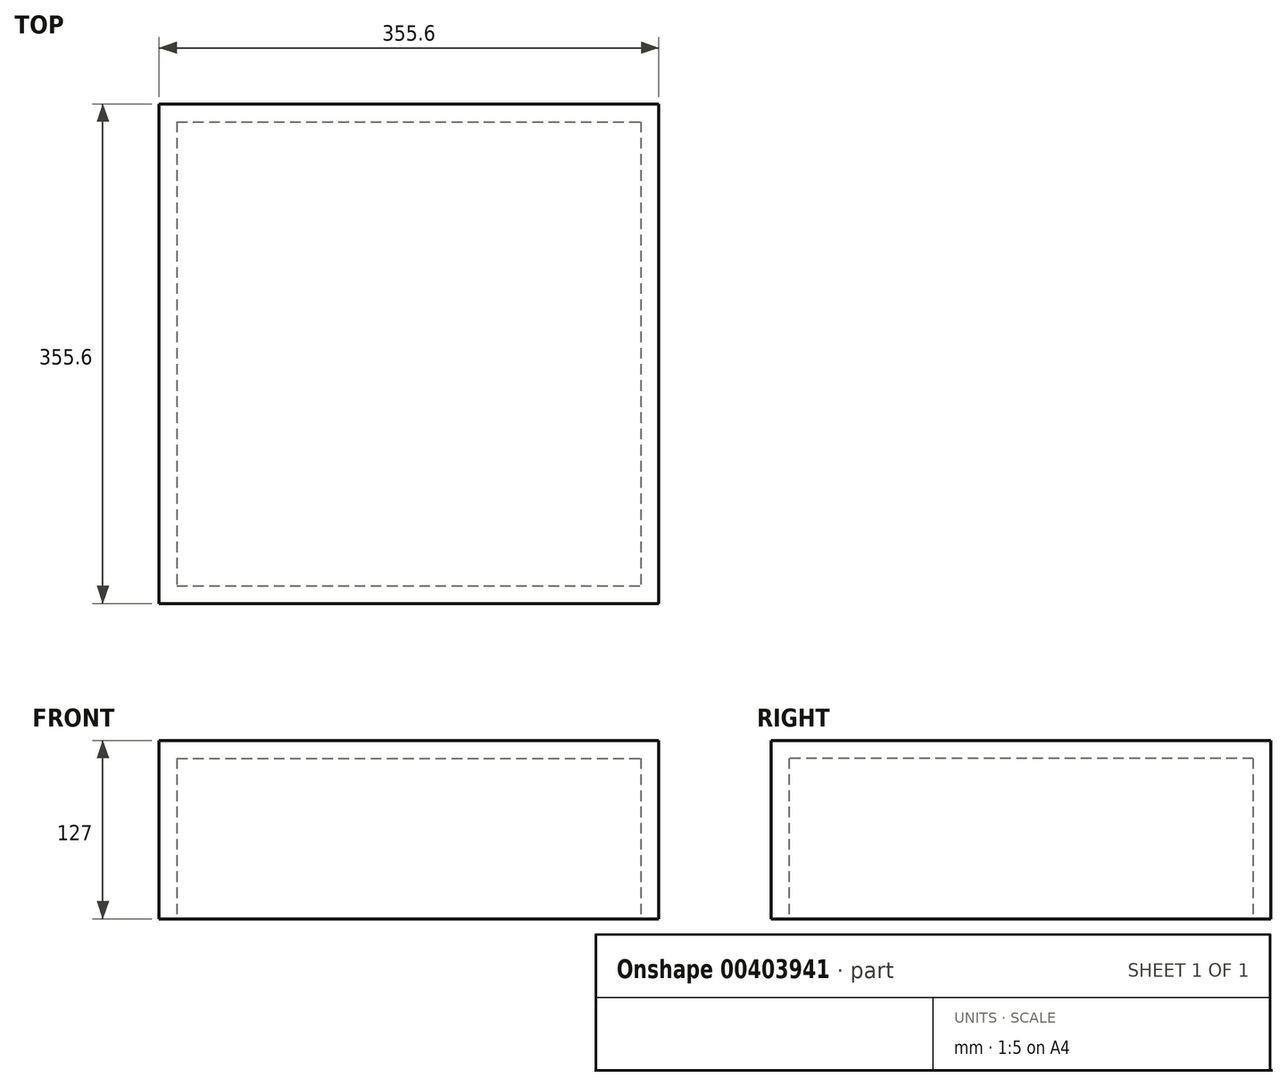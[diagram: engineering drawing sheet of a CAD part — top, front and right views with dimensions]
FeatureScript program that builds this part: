
annotation { "Feature Type Name" : "Feature", "Feature Type Description" : "" }
export const myFeature = defineFeature(function(context is Context, id is Id, definition is map)
    precondition{}
    {
        {
            var Q0;
            Q0=qCreatedBy(makeId("Top.planeOp"),FACE);
            var sketch = newSketch(context, id + "F0", { "sketchPlane" : qUnion([Q0])});
            skLineSegment(sketch, "E0.bottom", {"start": v(-177.8, 177.8) * mm, "end": v(177.8, 177.8) * mm});
            skLineSegment(sketch, "E0.top", {"start": v(-177.8, -177.8) * mm, "end": v(177.8, -177.8) * mm});
            skLineSegment(sketch, "E0.left", {"start": v(-177.8, 177.8) * mm, "end": v(-177.8, -177.8) * mm});
            skLineSegment(sketch, "E0.right", {"start": v(177.8, 177.8) * mm, "end": v(177.8, -177.8) * mm});
            skPoint(sketch, "E0.middle", {"position": v(0, 0) * mm});
            skSolve(sketch);
        }
        {
            var Q0;
            Q0=makeQuery(id+"F0.imprint","IMPRINT",FACE,{"disambiguationData":[TD([[makeQuery(id+"F0.imprint","IMPRINT",EDGE,{"derivedFrom":sQuery(id+"F0.wireOp",EDGE,"E0.bottom")}),-1.0]])]});
            var Q1;
            Q1 = qSketchRegion(id + "F2", true);
            extrude(context, id + "F1", {"entities" : qUnion([Q0, Q1]), "depth" : 127 * mm});
        }
        {
            var Q0;
            Q0=qCreatedBy(makeId("Top.planeOp"),FACE);
            var sketch = newSketch(context, id + "F2", { "sketchPlane" : qUnion([Q0])});
            skLineSegment(sketch, "E1.bottom", {"start": v(-165.1, 165.1) * mm, "end": v(165.1, 165.1) * mm});
            skLineSegment(sketch, "E1.top", {"start": v(-165.1, -165.1) * mm, "end": v(165.1, -165.1) * mm});
            skLineSegment(sketch, "E1.left", {"start": v(-165.1, 165.1) * mm, "end": v(-165.1, -165.1) * mm});
            skLineSegment(sketch, "E1.right", {"start": v(165.1, 165.1) * mm, "end": v(165.1, -165.1) * mm});
            skPoint(sketch, "E1.middle", {"position": v(0, 0) * mm});
            skSolve(sketch);
        }
        {
            var Q0;
            Q0 = qSketchRegion(id + "F2", true);
            extrude(context, id + "F3", {"entities" : qUnion([Q0]), "operationType" : NewBodyOperationType.REMOVE, "depth" : 114.3 * mm});
        }
    });
